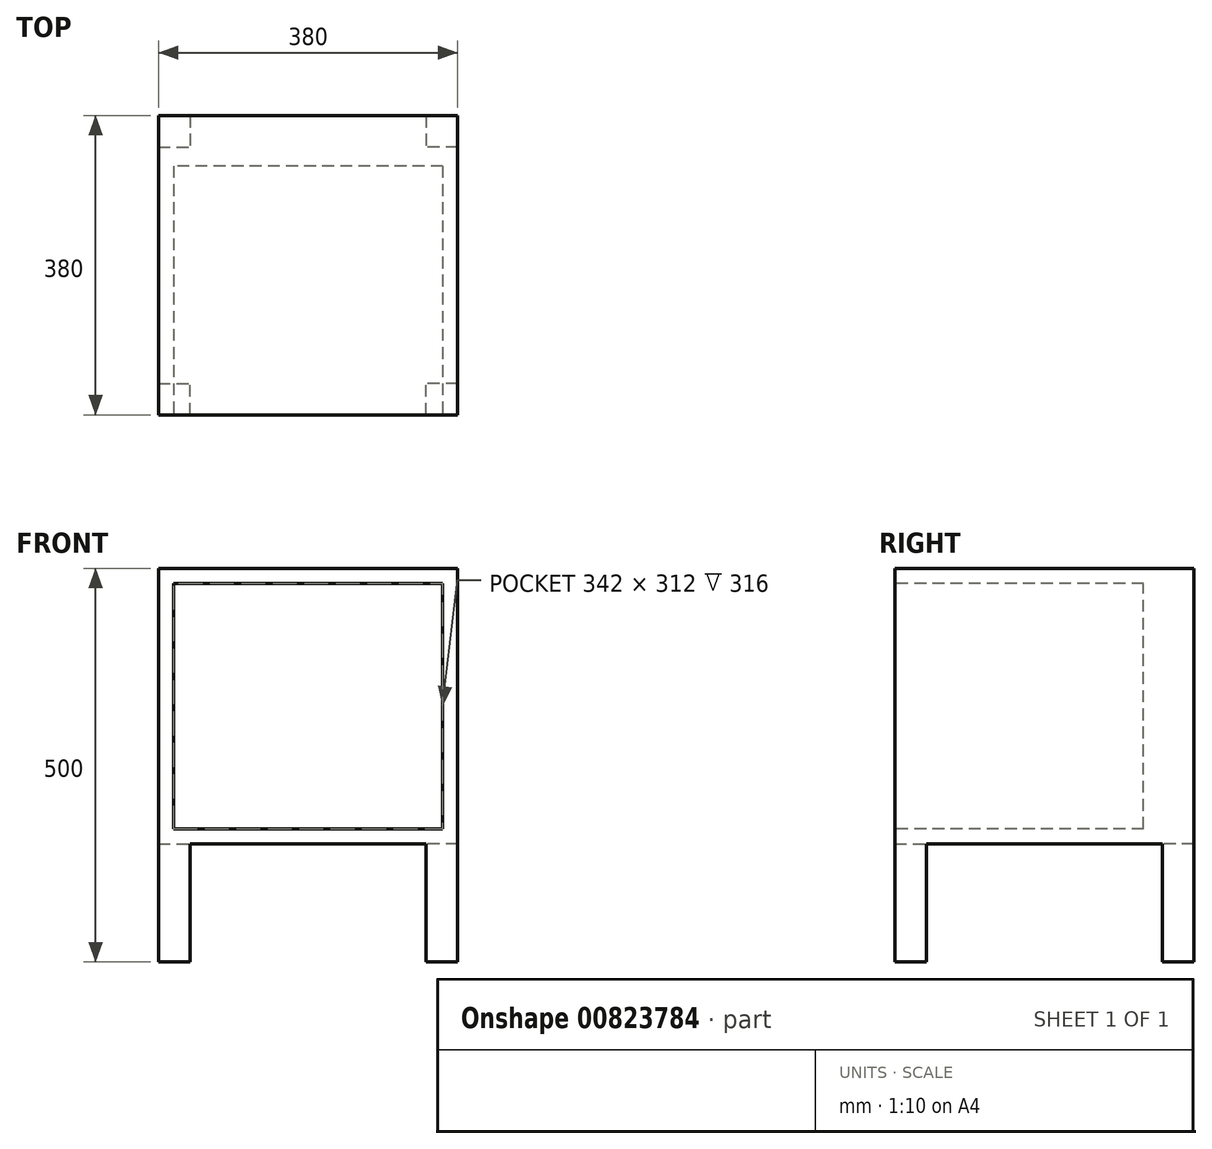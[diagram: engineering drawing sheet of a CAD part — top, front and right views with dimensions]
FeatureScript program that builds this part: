
annotation { "Feature Type Name" : "Feature", "Feature Type Description" : "" }
export const myFeature = defineFeature(function(context is Context, id is Id, definition is map)
    precondition{}
    {
        {
            var Q0;
            Q0=qCreatedBy(makeId("Top.planeOp"),FACE);
            var sketch = newSketch(context, id + "F0", { "sketchPlane" : qUnion([Q0])});
            skLineSegment(sketch, "E0.bottom", {"start": v(190, -190) * mm, "end": v(-190, -190) * mm});
            skLineSegment(sketch, "E0.top", {"start": v(190, 190) * mm, "end": v(-190, 190) * mm});
            skLineSegment(sketch, "E0.left", {"start": v(190, -190) * mm, "end": v(190, 190) * mm});
            skLineSegment(sketch, "E0.right", {"start": v(-190, -190) * mm, "end": v(-190, 190) * mm});
            skPoint(sketch, "E0.middle", {"position": v(0, 0) * mm});
            skSolve(sketch);
        }
        {
            var Q0;
            Q0 = qSketchRegion(id + "F0", true);
            extrude(context, id + "F1", {"entities" : qUnion([Q0]), "depth" : 350 * mm, "offsetDistance" : 25 * mm});
        }
        {
            var Q0;
            Q0=makeQuery(id+"F1.opExtrude","SWEPT_FACE",FACE,{"disambiguationData":[OSD([sQuery(id+"F0.wireOp",EDGE,"E0.bottom")])]});
            var sketch = newSketch(context, id + "F2", { "sketchPlane" : qUnion([Q0])});
            skLineSegment(sketch, "E1.bottom", {"start": v(171, 19) * mm, "end": v(-171, 19) * mm});
            skLineSegment(sketch, "E1.top", {"start": v(171, 331) * mm, "end": v(-171, 331) * mm});
            skLineSegment(sketch, "E1.left", {"start": v(171, 19) * mm, "end": v(171, 331) * mm});
            skLineSegment(sketch, "E1.right", {"start": v(-171, 19) * mm, "end": v(-171, 331) * mm});
            skPoint(sketch, "E1.middle", {"position": v(0, 175) * mm});
            skPoint(sketch, "E1.middle.positionSnap0", {"position": v(190, 175) * mm});
            skPoint(sketch, "E1.centerSnap0", {"position": v(190, 175) * mm});
            skSolve(sketch);
        }
        {
            var Q0;
            Q0=makeQuery(id+"F2.imprint","IMPRINT",FACE,{"disambiguationData":[TD([[makeQuery(id+"F2.imprint","IMPRINT",EDGE,{"derivedFrom":sQuery(id+"F2.wireOp",EDGE,"E1.bottom")}),-1.0]])]});
            extrude(context, id + "F3", {"entities" : qUnion([Q0]), "operationType" : NewBodyOperationType.REMOVE, "oppositeDirection" : true, "depth" : 316 * mm, "offsetDistance" : 25 * mm});
        }
        {
            var Q0;
            Q0=makeQuery(id+"F1.opExtrude","CAP_FACE",FACE,{"disambiguationData":[OSD([sQuery(id+"F0.wireOp",EDGE,"E0.bottom"),sQuery(id+"F0.wireOp",EDGE,"E0.top"),sQuery(id+"F0.wireOp",EDGE,"E0.left"),sQuery(id+"F0.wireOp",EDGE,"E0.right")])],"isStart":true});
            var sketch = newSketch(context, id + "F4", { "sketchPlane" : qUnion([Q0])});
            skLineSegment(sketch, "E2.bottom", {"start": v(190, 190) * mm, "end": v(150, 190) * mm});
            skLineSegment(sketch, "E2.top", {"start": v(190, 150) * mm, "end": v(150, 150) * mm});
            skLineSegment(sketch, "E2.left", {"start": v(190, 190) * mm, "end": v(190, 150) * mm});
            skLineSegment(sketch, "E2.right", {"start": v(150, 190) * mm, "end": v(150, 150) * mm});
            skLineSegment(sketch, "E3.bottom", {"start": v(-190, 190) * mm, "end": v(-150, 190) * mm});
            skLineSegment(sketch, "E3.top", {"start": v(-190, 150) * mm, "end": v(-150, 150) * mm});
            skLineSegment(sketch, "E3.left", {"start": v(-190, 190) * mm, "end": v(-190, 150) * mm});
            skLineSegment(sketch, "E3.right", {"start": v(-150, 190) * mm, "end": v(-150, 150) * mm});
            skLineSegment(sketch, "E4.bottom", {"start": v(-190, -190) * mm, "end": v(-150, -190) * mm});
            skLineSegment(sketch, "E4.top", {"start": v(-190, -150) * mm, "end": v(-150, -150) * mm});
            skLineSegment(sketch, "E4.left", {"start": v(-190, -190) * mm, "end": v(-190, -150) * mm});
            skLineSegment(sketch, "E4.right", {"start": v(-150, -190) * mm, "end": v(-150, -150) * mm});
            skLineSegment(sketch, "E5.bottom", {"start": v(190, -190) * mm, "end": v(150, -190) * mm});
            skLineSegment(sketch, "E5.top", {"start": v(190, -150) * mm, "end": v(150, -150) * mm});
            skLineSegment(sketch, "E5.left", {"start": v(190, -190) * mm, "end": v(190, -150) * mm});
            skLineSegment(sketch, "E5.right", {"start": v(150, -190) * mm, "end": v(150, -150) * mm});
            skSolve(sketch);
        }
        {
            var Q0;
            Q0=makeQuery(id+"F4.imprint","IMPRINT",FACE,{"disambiguationData":[TD([[makeQuery(id+"F4.imprint","IMPRINT",EDGE,{"derivedFrom":sQuery(id+"F4.wireOp",EDGE,"E2.bottom")}),1.0]])]});
            var Q1;
            Q1=makeQuery(id+"F4.imprint","IMPRINT",FACE,{"disambiguationData":[TD([[makeQuery(id+"F4.imprint","IMPRINT",EDGE,{"derivedFrom":sQuery(id+"F4.wireOp",EDGE,"E4.bottom")}),-1.0]])]});
            var Q2;
            Q2=makeQuery(id+"F4.imprint","IMPRINT",FACE,{"disambiguationData":[TD([[makeQuery(id+"F4.imprint","IMPRINT",EDGE,{"derivedFrom":sQuery(id+"F4.wireOp",EDGE,"E5.bottom")}),-1.0]])]});
            var Q3;
            Q3=makeQuery(id+"F4.imprint","IMPRINT",FACE,{"disambiguationData":[TD([[makeQuery(id+"F4.imprint","IMPRINT",EDGE,{"derivedFrom":sQuery(id+"F4.wireOp",EDGE,"E3.bottom")}),1.0]])]});
            extrude(context, id + "F5", {"entities" : qUnion([Q0, Q1, Q2, Q3]), "operationType" : NewBodyOperationType.ADD, "depth" : 150 * mm, "offsetDistance" : 25 * mm});
        }
    });
